# Revit family: F161-38X18
name_source: partatom
category: Furniture Systems
units: mm (PartAtom-declared; Revit-internal decimal feet)

## family parameters
Always vertical = Yes
Cut with Voids When Loaded = No
Part Type = Normal
Room Calculation Point = No
Round Connector Dimension = Use Diameter
Shared = No
Work Plane-Based = No

## types (8) — shared parameters
3" Rectangle Leg = <By Category>
6" Rectangle Leg = <By Category>
Base = <By Category>
Caster = Default New Material(1)
Description = Lotus Series - Medium Gear
Glide = <By Category>
Low Profile = Black
Manufacturer = FOMCORE
Mod Leg = <By Category>
Model = F161-38X18
Seat Fabric = <By Category>
Side Fabric = <By Category>
Triangle Leg = <By Category>
URL = https://fomcore.com

## per-type parameters (varying)
| type | C3 | C6 | G1 | L1 | LEG H | LEG OPTIONS | M6 | R3 | R6 | T6 |
| F161-38X18-C3 | Yes | No | No | No | 0' - 3 1/2" | 1 | No | No | No | No |
| F161-38X18-C6 | No | Yes | No | No | 0' - 6 1/2" | 2 | No | No | No | No |
| F161-38X18-G1 | No | No | Yes | No | 0' - 1 1/2" | 3 | No | No | No | No |
| F161-38X18-L1 | No | No | No | Yes | 0' - 1 1/2" | 4 | No | No | No | No |
| F161-38X18-M6 | No | No | No | No | 0' - 6 1/2" | 5 | Yes | No | No | No |
| F161-38X18-R3 | No | No | No | No | 0' - 3 1/2" | 6 | No | Yes | No | No |
| F161-38X18-R6 | No | No | No | No | 0' - 6 1/2" | 7 | No | No | Yes | No |
| F161-38X18-T6 | No | No | No | No | 0' - 6 1/2" | 8 | No | No | No | Yes |

## geometry (parser evidence)
native form markers: Sweep x3
no freeform markers — native parametric forms only
